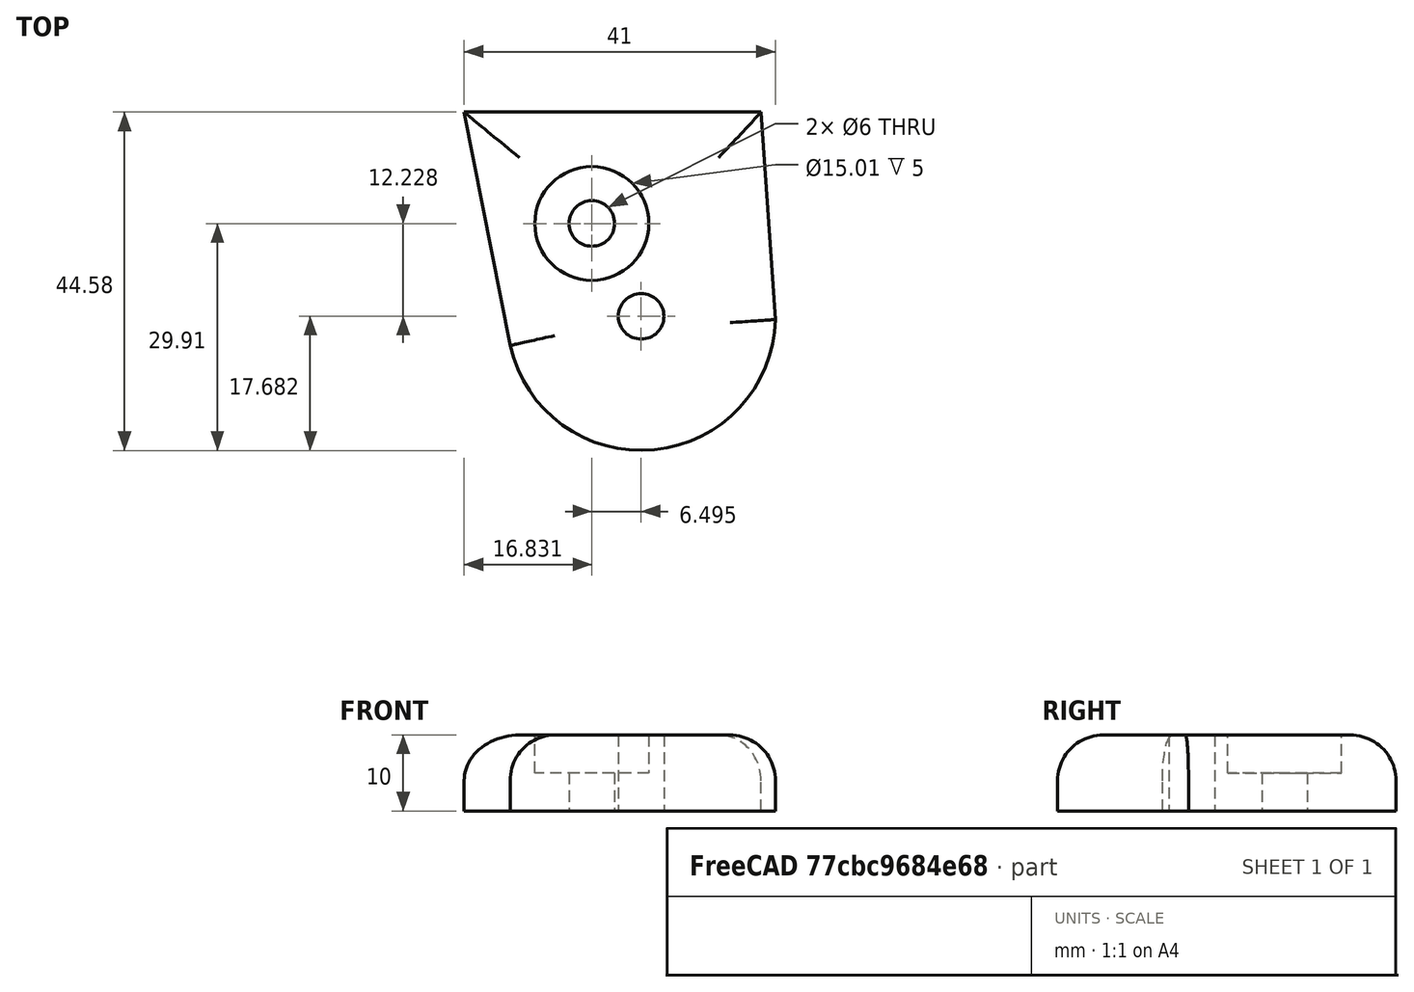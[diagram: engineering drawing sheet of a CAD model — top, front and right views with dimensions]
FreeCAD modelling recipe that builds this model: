
FCSTD DOCUMENT  (FreeCAD 0.19R19327 (Git))
Label: smallblob
License: All rights reserved
LicenseURL: http://en.wikipedia.org/wiki/All_rights_reserved
objects: Sketcher::SketchObject×2, PartDesign::Pad×1, PartDesign::Fillet×1, PartDesign::Pocket×1, PartDesign::Hole×1, PartDesign::Body×1
note: 10 computed .brp shape members not serialized (recipe doc carries the construction recipe); baked Part::Feature solids carry a one-line shape summary decoded from their .brp

FEATURE [Sketcher::SketchObject] Sketch
  MapMode = 5
  Support = -> [XY_Plane]
  sketch-geometry (4):
    g0: LineSegment StartX=-44.0206 StartY=10.2139 StartZ=0 EndX=-4.89117 EndY=10.2139 EndZ=0
    g1: LineSegment StartX=-4.89117 StartY=10.2139 StartZ=0 EndX=-3.02102 EndY=-17.1191 EndZ=0
    g2: ArcOfCircle CenterX=-20.694 CenterY=-16.6875 CenterZ=0 NormalX=0 NormalY=0 NormalZ=1 AngleXU=0 Radius=17.6782 StartAngle=3.36158 EndAngle=6.25877
    g3: LineSegment StartX=-44.0206 StartY=10.2139 StartZ=0 EndX=-37.9461 EndY=-20.5453 EndZ=0
  constraints (4):
    c: Horizontal(g0)
    c: Coincident(g1,g0)
    c: Coincident(g2,g1)
    c: Coincident(g3,g2)
FEATURE [PartDesign::Pad] Pad
  Length = 10
  Length2 = 100
  Profile = -> Sketch
  Type = 0
FEATURE [PartDesign::Fillet] Fillet
  Base = -> Pad [Edge4,Edge7]
  BaseFeature = -> Pad
  Radius = 6
FEATURE [Sketcher::SketchObject] Sketch001
  MapMode = 5
  Placement = pos=(0,0,10) rot=(0,0,1;0rad)
  Support = -> [Fillet]
  sketch-geometry (1):
    g0: Circle CenterX=-27.1892 CenterY=-4.4596 CenterZ=0 NormalX=0 NormalY=0 NormalZ=1 AngleXU=0 Radius=7.50272
FEATURE [PartDesign::Pocket] Pocket
  BaseFeature = -> Fillet
  Length = 5
  Length2 = 100
  Profile = -> Sketch001
  Type = 0
FEATURE [PartDesign::Hole] Hole
  BaseFeature = -> Pocket
  Depth = 25
  DepthType = 0
  Diameter = 6
  DrillPoint = 1
  DrillPointAngle = 118
  HoleCutCountersinkAngle = 90
  HoleCutDepth = 0
  HoleCutDiameter = 0
  HoleCutType = 0
  ModelActualThread = false
  Profile = -> Pocket [Face8]
  Tapered = false
  TaperedAngle = 90
  ThreadAngle = 0
  ThreadClass = 0
  ThreadCutOffInner = 0
  ThreadCutOffOuter = 0
  ThreadDirection = 0
  ThreadFit = 0
  ThreadPitch = 0
  ThreadSize = 0
  ThreadType = 0
  Threaded = false
FEATURE [PartDesign::Body] Body
  Group = -> [Sketch,Pad,Fillet,Sketch001,Pocket,Hole]
  Origin = -> Origin
  Tip = -> Hole
